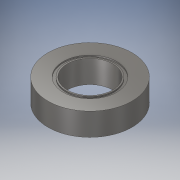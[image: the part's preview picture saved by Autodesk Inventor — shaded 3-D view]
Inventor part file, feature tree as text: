
AUTODESK INVENTOR PART (.ipt)
format: ipt  version: 2018 (Build 220112000, 112)  size: 184,832 bytes
history: native  units: in
note: dims shown in document units (in); Inventor stores cm internally (conversion verified against a paired STEP export)
features: sketch x5, extrude x4, hole x1, chamfer x1, pattern_circular x1
ambient origin geometry x8: Origin, YZ Plane, XZ Plane, XY Plane, X Axis, Y Axis, Z Axis, Center Point
bodies: Solid1 (feature_tree)
feature tree (12):
  extrude  "Extrusion1"  Depth=0.5in TaperAngle=0.0deg
  extrude  "Extrusion2"  Depth=0.03in
  extrude  "Extrusion3"  Depth=0.03in
  extrude  "Extrusion4"  Depth=0.03in
  hole  "Hole1"  [1 undecoded]
  chamfer  "Chamfer1"  Distance=0.68in
  pattern_circular  "Circular Pattern1"  Angle=45.0deg  [1 undecoded]
  sketch  "Sketch1"  dims[d0=1.85in d1=0.5in d2=0.0in]
  sketch  "Sketch2"  dims[d3=0.03in d4=0.06in]
  sketch  "Sketch3"  dims[d5=0.03in d6=0.0in d7=1.0in]
  sketch  "Sketch4"  dims[d8=0.05in d9=0.0in d10=0.03in]
  sketch  "Sketch5"  dims[d11=0.06in d12=0.03in d13=0.0in d14=0.68in d15=45.0deg d16=0.13in d17=0.328in d18=0.375in d19=0.25in d20=0.5635in d21=0.4in d22=0.8108in d23=2.3622in d24=360.0deg d26=0.015in d27=0.125in d28=45.0deg]
note: 2 required parameter values undecoded (feature->parameter linkage not recoverable at this tier; creation-order binding heuristic only, values carry confidence <= 0.55)
